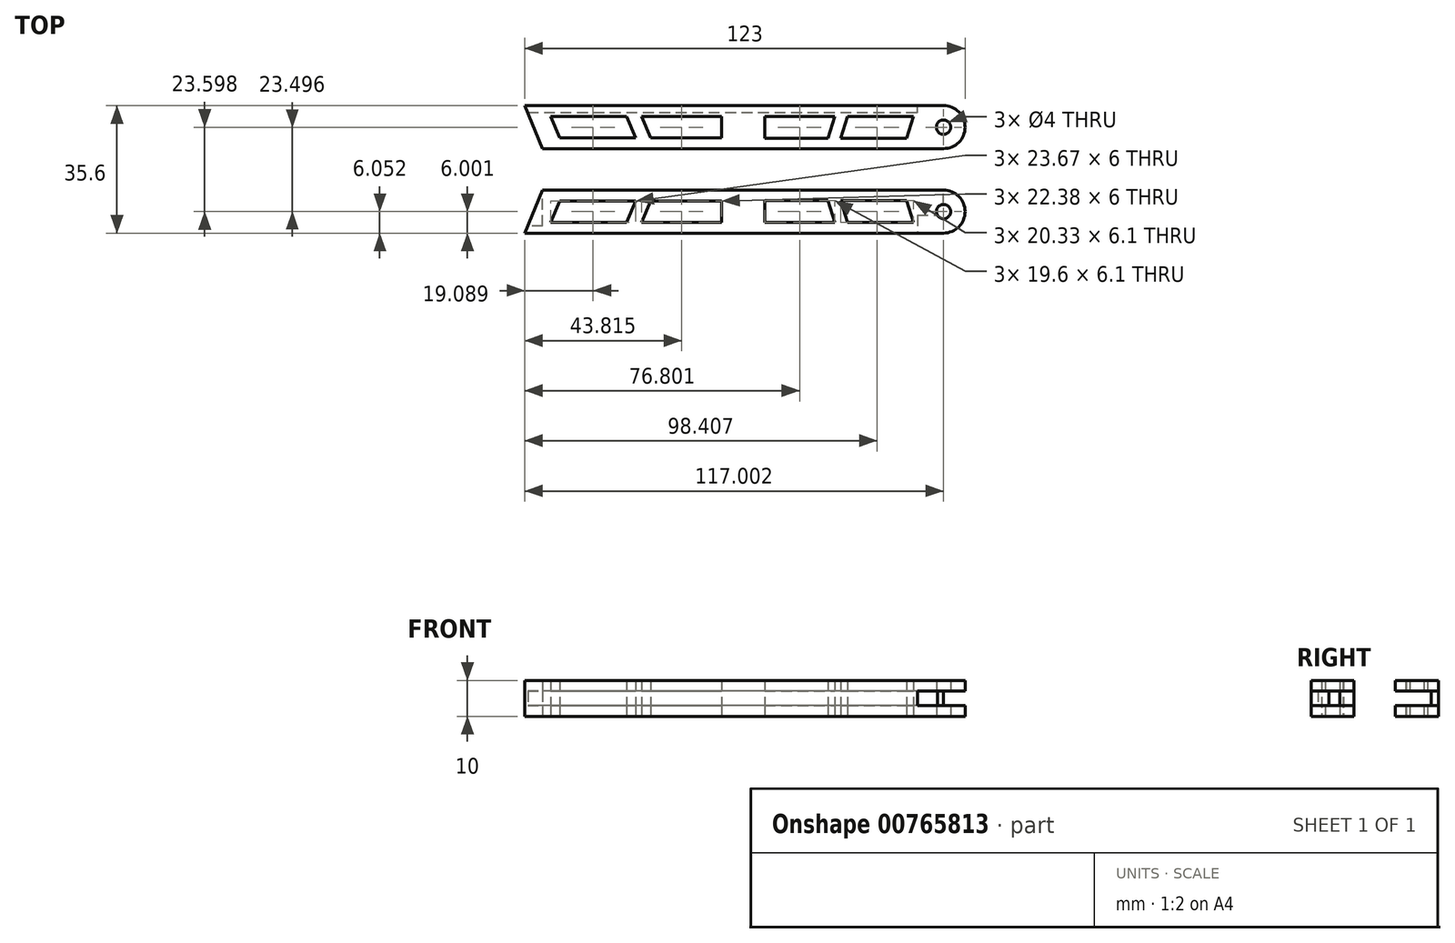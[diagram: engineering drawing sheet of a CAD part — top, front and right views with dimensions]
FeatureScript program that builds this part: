
annotation { "Feature Type Name" : "Feature", "Feature Type Description" : "" }
export const myFeature = defineFeature(function(context is Context, id is Id, definition is map)
    precondition{}
    {
        {
            var Q0;
            Q0=qCreatedBy(makeId("Top.planeOp"),FACE);
            var sketch = newSketch(context, id + "F0", { "sketchPlane" : qUnion([Q0])});
            skCircle(sketch, "E0", {"center": v(38.71, 11.8) * mm, "radius": 2 * mm});
            skArc(sketch, "E1", {"start": v(38.71, 5.8) * mm, "mid": v(44.71, 11.8) * mm, "end": v(38.71, 17.8) * mm});
            skLineSegment(sketch, "E2", {"start": v(38.71, 17.8) * mm, "end": v(-78.29, 17.8) * mm});
            skLineSegment(sketch, "E3", {"start": v(-78.29, 17.8) * mm, "end": v(-73.29, 5.8) * mm});
            skLineSegment(sketch, "E4", {"start": v(-68.54, 8.8) * mm, "end": v(-71.04, 14.8) * mm});
            skLineSegment(sketch, "E5.trimOffspring", {"start": v(-11.29, 14.8) * mm, "end": v(8.3, 14.8) * mm});
            skLineSegment(sketch, "E6", {"start": v(38.71, 5.8) * mm, "end": v(-73.29, 5.8) * mm});
            skLineSegment(sketch, "E7", {"start": v(-23.29, 14.8) * mm, "end": v(-23.29, 8.8) * mm});
            skLineSegment(sketch, "E8", {"start": v(-68.54, 8.8) * mm, "end": v(-47.37, 8.8) * mm});
            skLineSegment(sketch, "E9", {"start": v(-71.04, 14.8) * mm, "end": v(-49.87, 14.8) * mm});
            skLineSegment(sketch, "E10.trimOffspring", {"start": v(-45.66, 14.8) * mm, "end": v(-23.29, 14.8) * mm});
            skLineSegment(sketch, "E11.trimOffspring", {"start": v(-43.16, 8.8) * mm, "end": v(-23.29, 8.8) * mm});
            skLineSegment(sketch, "E12", {"start": v(-49.87, 14.8) * mm, "end": v(-47.37, 8.8) * mm});
            skLineSegment(sketch, "E13", {"start": v(-45.66, 14.8) * mm, "end": v(-43.16, 8.8) * mm});
            skPoint(sketch, "E14.end.orphan", {"position": v(30.28, 14.64) * mm});
            skLineSegment(sketch, "E15.trimOffspring", {"start": v(11.86, 14.8) * mm, "end": v(30.28, 14.8) * mm});
            skLineSegment(sketch, "E16", {"start": v(28.37, 8.7) * mm, "end": v(30.28, 14.8) * mm});
            skLineSegment(sketch, "E17", {"start": v(28.37, 8.7) * mm, "end": v(9.95, 8.7) * mm});
            skLineSegment(sketch, "E18", {"start": v(8.3, 14.8) * mm, "end": v(6.4, 8.7) * mm});
            skLineSegment(sketch, "E19", {"start": v(9.95, 8.7) * mm, "end": v(11.86, 14.8) * mm});
            skLineSegment(sketch, "E20", {"start": v(6.4, 8.7) * mm, "end": v(-11.29, 8.7) * mm});
            skLineSegment(sketch, "E21", {"start": v(-11.29, 14.8) * mm, "end": v(-11.29, 8.7) * mm});
            skLineSegment(sketch, "E22", {"start": v(-93.43, 0) * mm, "end": v(79.33, 0) * mm});
            skLineSegment(sketch, "E23.MirrorCS", {"start": v(-45.66, -14.8) * mm, "end": v(-43.16, -8.8) * mm});
            skCircle(sketch, "E24.MirrorC", {"center": v(38.71, -11.8) * mm, "radius": 2 * mm});
            skLineSegment(sketch, "E25.MirrorCS", {"start": v(-11.29, -14.8) * mm, "end": v(-11.29, -8.7) * mm});
            skLineSegment(sketch, "E26.MirrorCS", {"start": v(28.37, -8.7) * mm, "end": v(30.28, -14.8) * mm});
            skLineSegment(sketch, "E27.MirrorCS", {"start": v(-23.29, -14.8) * mm, "end": v(-23.29, -8.8) * mm});
            skLineSegment(sketch, "E28.MirrorCS", {"start": v(8.3, -14.8) * mm, "end": v(6.4, -8.7) * mm});
            skLineSegment(sketch, "E29.MirrorCS", {"start": v(-49.87, -14.8) * mm, "end": v(-47.37, -8.8) * mm});
            skLineSegment(sketch, "E30.MirrorCS", {"start": v(9.95, -8.7) * mm, "end": v(11.86, -14.8) * mm});
            skLineSegment(sketch, "E31.MirrorCS", {"start": v(-68.54, -8.8) * mm, "end": v(-71.04, -14.8) * mm});
            skLineSegment(sketch, "E32.MirrorCS", {"start": v(-45.66, -14.8) * mm, "end": v(-23.29, -14.8) * mm});
            skLineSegment(sketch, "E33.MirrorCS", {"start": v(28.37, -8.7) * mm, "end": v(9.95, -8.7) * mm});
            skLineSegment(sketch, "E34.MirrorCS", {"start": v(-78.29, -17.8) * mm, "end": v(-73.29, -5.8) * mm});
            skLineSegment(sketch, "E35.MirrorCS", {"start": v(-43.16, -8.8) * mm, "end": v(-23.29, -8.8) * mm});
            skLineSegment(sketch, "E36.MirrorCS", {"start": v(11.86, -14.8) * mm, "end": v(30.28, -14.8) * mm});
            skLineSegment(sketch, "E37.MirrorCS", {"start": v(38.71, -17.8) * mm, "end": v(-78.29, -17.8) * mm});
            skLineSegment(sketch, "E38.MirrorCS", {"start": v(-68.54, -8.8) * mm, "end": v(-47.37, -8.8) * mm});
            skLineSegment(sketch, "E39.MirrorCS", {"start": v(38.71, -5.8) * mm, "end": v(-73.29, -5.8) * mm});
            skLineSegment(sketch, "E40.MirrorCS", {"start": v(-11.29, -14.8) * mm, "end": v(8.3, -14.8) * mm});
            skLineSegment(sketch, "E41.MirrorCS", {"start": v(6.4, -8.7) * mm, "end": v(-11.29, -8.7) * mm});
            skLineSegment(sketch, "E42.MirrorCS", {"start": v(-71.04, -14.8) * mm, "end": v(-49.87, -14.8) * mm});
            skPoint(sketch, "E43.MirrorP", {"position": v(30.28, -14.64) * mm});
            skArc(sketch, "E44.MirrorCS", {"start": v(38.71, -5.8) * mm, "mid": v(44.71, -11.8) * mm, "end": v(38.71, -17.8) * mm});
            skSolve(sketch);
        }
        {
            var Q0;
            Q0=makeQuery(id+"F0.imprint","IMPRINT",FACE,{"disambiguationData":[TD([[makeQuery(id+"F0.imprint","IMPRINT",EDGE,{"derivedFrom":sQuery(id+"F0.wireOp",EDGE,"E0")}),-1.0]])]});
            var Q1;
            Q1=makeQuery(id+"F0.imprint","IMPRINT",FACE,{"disambiguationData":[TD([[makeQuery(id+"F0.imprint","IMPRINT",EDGE,{"derivedFrom":sQuery(id+"F0.wireOp",EDGE,"E23.MirrorCS")}),1.0]])]});
            extrude(context, id + "F1", {"entities" : qUnion([Q0, Q1]), "depth" : 10 * mm, "offsetDistance" : 25 * mm});
        }
        {
            var Q0;
            Q0=makeQuery(id+"F1.opExtrude","SWEPT_FACE",FACE,{"disambiguationData":[OSD([sQuery(id+"F0.wireOp",EDGE,"E6")])]});
            var sketch = newSketch(context, id + "F2", { "sketchPlane" : qUnion([Q0])});
            skLineSegment(sketch, "E45", {"start": v(-70.05, 7) * mm, "end": v(-73.29, 7) * mm});
            skPoint(sketch, "E45.endSnap0", {"position": v(-73.29, 5) * mm});
            skLineSegment(sketch, "E46", {"start": v(-70.05, 7) * mm, "end": v(38.71, 7) * mm});
            skLineSegment(sketch, "E47", {"start": v(-72.79, 2.97) * mm, "end": v(-73.29, 2.97) * mm});
            skLineSegment(sketch, "E48", {"start": v(-72.79, 2.97) * mm, "end": v(38.71, 2.97) * mm});
            skLineSegment(sketch, "E49", {"start": v(38.71, 7) * mm, "end": v(48.9, 7) * mm});
            skLineSegment(sketch, "E50", {"start": v(38.71, 2.97) * mm, "end": v(48.9, 2.97) * mm});
            skLineSegment(sketch, "E51", {"start": v(48.9, 2.97) * mm, "end": v(48.9, 7) * mm});
            skLineSegment(sketch, "E52", {"start": v(-73.29, 7) * mm, "end": v(-77.6, 7) * mm});
            skLineSegment(sketch, "E53", {"start": v(-73.29, 2.97) * mm, "end": v(-78.65, 2.97) * mm});
            skLineSegment(sketch, "E54", {"start": v(-77.6, 7) * mm, "end": v(-78.65, 7) * mm});
            skLineSegment(sketch, "E55", {"start": v(-78.65, 2.97) * mm, "end": v(-78.65, 7) * mm});
            skSolve(sketch);
        }
        {
            var Q0;
            {var subQ1=sQuery(id+"F2.wireOp",EDGE,"E52");Q0=makeQuery(id+"F2.imprint","IMPRINT",FACE,{"disambiguationData":[TD([[makeQuery(id+"F2.imprint","IMPRINT",EDGE,{"derivedFrom":subQ1}),1.0]])]});}
            var Q1;
            {var subQ3=sQuery(id+"F2.wireOp",EDGE,"E45");Q1=makeQuery(id+"F2.imprint","IMPRINT",FACE,{"disambiguationData":[TD([[makeQuery(id+"F2.imprint","IMPRINT",EDGE,{"derivedFrom":subQ3}),1.0]])]});}
            var Q2;
            {var subQ0=sQuery(id+"F2.wireOp",EDGE,"E49");Q2=makeQuery(id+"F2.imprint","IMPRINT",FACE,{"disambiguationData":[TD([[makeQuery(id+"F2.imprint","IMPRINT",EDGE,{"derivedFrom":subQ0}),-1.0]])]});}
            extrude(context, id + "F3", {"entities" : qUnion([Q0, Q1, Q2]), "operationType" : NewBodyOperationType.REMOVE, "oppositeDirection" : true, "depth" : 10 * mm, "offsetDistance" : 25 * mm});
        }
        {
            var Q0;
            Q0=makeQuery(id+"F1.opExtrude","SWEPT_FACE",FACE,{"disambiguationData":[OSD([sQuery(id+"F0.wireOp",EDGE,"E2")])]});
            var sketch = newSketch(context, id + "F4", { "sketchPlane" : qUnion([Q0])});
            skLineSegment(sketch, "E56", {"start": v(-31.3, 7) * mm, "end": v(-31.3, 3) * mm});
            skLineSegment(sketch, "E57", {"start": v(-35.96, 7) * mm, "end": v(-31.3, 7) * mm});
            skLineSegment(sketch, "E58", {"start": v(-36.15, 3) * mm, "end": v(-31.3, 3) * mm});
            skLineSegment(sketch, "E59", {"start": v(-36.15, 3) * mm, "end": v(-46.28, 3) * mm});
            skLineSegment(sketch, "E60", {"start": v(-35.96, 7) * mm, "end": v(-46.28, 7) * mm});
            skLineSegment(sketch, "E61", {"start": v(-46.28, 3) * mm, "end": v(-46.28, 7) * mm});
            skSolve(sketch);
        }
        {
            var Q0;
            {var subQ0=sQuery(id+"F4.wireOp",EDGE,"E61");Q0=makeQuery(id+"F4.imprint","IMPRINT",FACE,{"disambiguationData":[TD([[makeQuery(id+"F4.imprint","IMPRINT",EDGE,{"derivedFrom":subQ0}),-1.0]])]});}
            var Q1;
            Q1=makeQuery(id+"F4.imprint","IMPRINT",FACE,{"disambiguationData":[TD([[makeQuery(id+"F4.imprint","IMPRINT",EDGE,{"derivedFrom":sQuery(id+"F4.wireOp",EDGE,"E56")}),-1.0]])]});
            extrude(context, id + "F5", {"entities" : qUnion([Q0, Q1]), "operationType" : NewBodyOperationType.REMOVE, "oppositeDirection" : true, "depth" : 5 * mm, "offsetDistance" : 25 * mm});
        }
        {
            var Q0;
            Q0=makeQuery(id+"F3.boolean.opBoolean","COPY",FACE,{"derivedFrom":makeQuery(id+"F3.opExtrude","CAP_FACE",FACE,{"disambiguationData":[OSD([sQuery(id+"F2.wireOp",EDGE,"E45"),sQuery(id+"F2.wireOp",EDGE,"E46"),sQuery(id+"F2.wireOp",EDGE,"E47"),sQuery(id+"F2.wireOp",EDGE,"E48"),sQuery(id+"F2.wireOp",EDGE,"E49"),sQuery(id+"F2.wireOp",EDGE,"E50"),sQuery(id+"F2.wireOp",EDGE,"E51"),sQuery(id+"F2.wireOp",EDGE,"E52"),sQuery(id+"F2.wireOp",EDGE,"E53"),sQuery(id+"F2.wireOp",EDGE,"E54"),sQuery(id+"F2.wireOp",EDGE,"E55")])],"isStart":false})});
            var sketch = newSketch(context, id + "F6", { "sketchPlane" : qUnion([Q0])});
            skLineSegment(sketch, "E62", {"start": v(31.3, 3) * mm, "end": v(31.3, 2.97) * mm});
            skSolve(sketch);
        }
        {
            var Q0;
            {var subQ0=sQuery(id+"F6.wireOp",EDGE,"E62");Q0=makeQuery(id+"F6.imprint","IMPRINT",FACE,{"disambiguationData":[TD([[makeQuery(id+"F6.imprint","IMPRINT",EDGE,{"derivedFrom":subQ0}),1.0]])]});}
            extrude(context, id + "F7", {"entities" : qUnion([Q0]), "operationType" : NewBodyOperationType.REMOVE, "oppositeDirection" : true, "depth" : 5 * mm, "offsetDistance" : 25 * mm});
        }
        {
            var Q0;
            Q0=makeQuery(id+"F1.opExtrude","SWEPT_FACE",FACE,{"disambiguationData":[OSD([sQuery(id+"F0.wireOp",EDGE,"E39.MirrorCS")])]});
            var sketch = newSketch(context, id + "F8", { "sketchPlane" : qUnion([Q0])});
            skLineSegment(sketch, "E63", {"start": v(-36.41, 7) * mm, "end": v(-60.81, 7) * mm});
            skLineSegment(sketch, "E64", {"start": v(-60.81, 7) * mm, "end": v(86.45, 7) * mm});
            skLineSegment(sketch, "E65", {"start": v(-35.59, 3) * mm, "end": v(-60.81, 3) * mm});
            skLineSegment(sketch, "E66", {"start": v(-60.81, 3) * mm, "end": v(86.7, 3) * mm});
            skLineSegment(sketch, "E67", {"start": v(86.7, 3) * mm, "end": v(86.45, 7) * mm});
            skLineSegment(sketch, "E68", {"start": v(-60.81, 3) * mm, "end": v(-60.81, 7) * mm});
            skSolve(sketch);
        }
        {
            var Q0;
            {var subQ5=sQuery(id+"F8.wireOp",EDGE,"E64");var subQ6=makeQuery(id+"F8.imprint","IMPRINT",VERTEX,{"derivedFrom":subQ5});Q0=makeQuery(id+"F8.imprint","IMPRINT",FACE,{"disambiguationData":[TD([[makeQuery(id+"F8.imprint","IMPRINT",EDGE,{"disambiguationData":[TD([[subQ6,1.0]])],"derivedFrom":subQ5}),-1.0]])]});}
            var Q1;
            {var subQ0=sQuery(id+"F8.wireOp",EDGE,"E68");Q1=makeQuery(id+"F8.imprint","IMPRINT",FACE,{"disambiguationData":[TD([[makeQuery(id+"F8.imprint","IMPRINT",EDGE,{"derivedFrom":subQ0}),-1.0]])]});}
            var Q2;
            {var subQ0=sQuery(id+"F8.wireOp",EDGE,"E67");Q2=makeQuery(id+"F8.imprint","IMPRINT",FACE,{"disambiguationData":[TD([[makeQuery(id+"F8.imprint","IMPRINT",EDGE,{"derivedFrom":subQ0}),1.0]])]});}
            extrude(context, id + "F9", {"entities" : qUnion([Q0, Q1, Q2]), "operationType" : NewBodyOperationType.REMOVE, "oppositeDirection" : true, "depth" : 10 * mm, "offsetDistance" : 25 * mm});
        }
        {
            var Q0;
            Q0=makeQuery(id+"F1.opExtrude","SWEPT_FACE",FACE,{"disambiguationData":[OSD([sQuery(id+"F0.wireOp",EDGE,"E37.MirrorCS")])]});
            var sketch = newSketch(context, id + "F10", { "sketchPlane" : qUnion([Q0])});
            skLineSegment(sketch, "E69", {"start": v(47.55, 3) * mm, "end": v(47.55, 7) * mm});
            skLineSegment(sketch, "E70", {"start": v(34.75, 3) * mm, "end": v(47.55, 3) * mm});
            skLineSegment(sketch, "E71", {"start": v(47.55, 3) * mm, "end": v(31.37, 3) * mm});
            skLineSegment(sketch, "E72", {"start": v(34.75, 7) * mm, "end": v(31.37, 7) * mm});
            skLineSegment(sketch, "E73", {"start": v(31.37, 7) * mm, "end": v(47.55, 7) * mm});
            skLineSegment(sketch, "E74", {"start": v(31.37, 7) * mm, "end": v(31.37, 3) * mm});
            skPoint(sketch, "E75.start.orphan", {"position": v(47.55, 10) * mm});
            skPoint(sketch, "E76.start.orphan", {"position": v(34.75, 10) * mm});
            skSolve(sketch);
        }
        {
            var Q0;
            {var subQ4=sQuery(id+"F10.wireOp",EDGE,"E74");Q0=makeQuery(id+"F10.imprint","IMPRINT",FACE,{"disambiguationData":[TD([[makeQuery(id+"F10.imprint","IMPRINT",EDGE,{"derivedFrom":subQ4}),1.0]])]});}
            var Q1;
            {var subQ0=sQuery(id+"F10.wireOp",EDGE,"E69");Q1=makeQuery(id+"F10.imprint","IMPRINT",FACE,{"disambiguationData":[TD([[makeQuery(id+"F10.imprint","IMPRINT",EDGE,{"derivedFrom":subQ0}),1.0]])]});}
            extrude(context, id + "F11", {"entities" : qUnion([Q0, Q1]), "operationType" : NewBodyOperationType.REMOVE, "oppositeDirection" : true, "depth" : 5 * mm, "offsetDistance" : 25 * mm});
        }
    });
